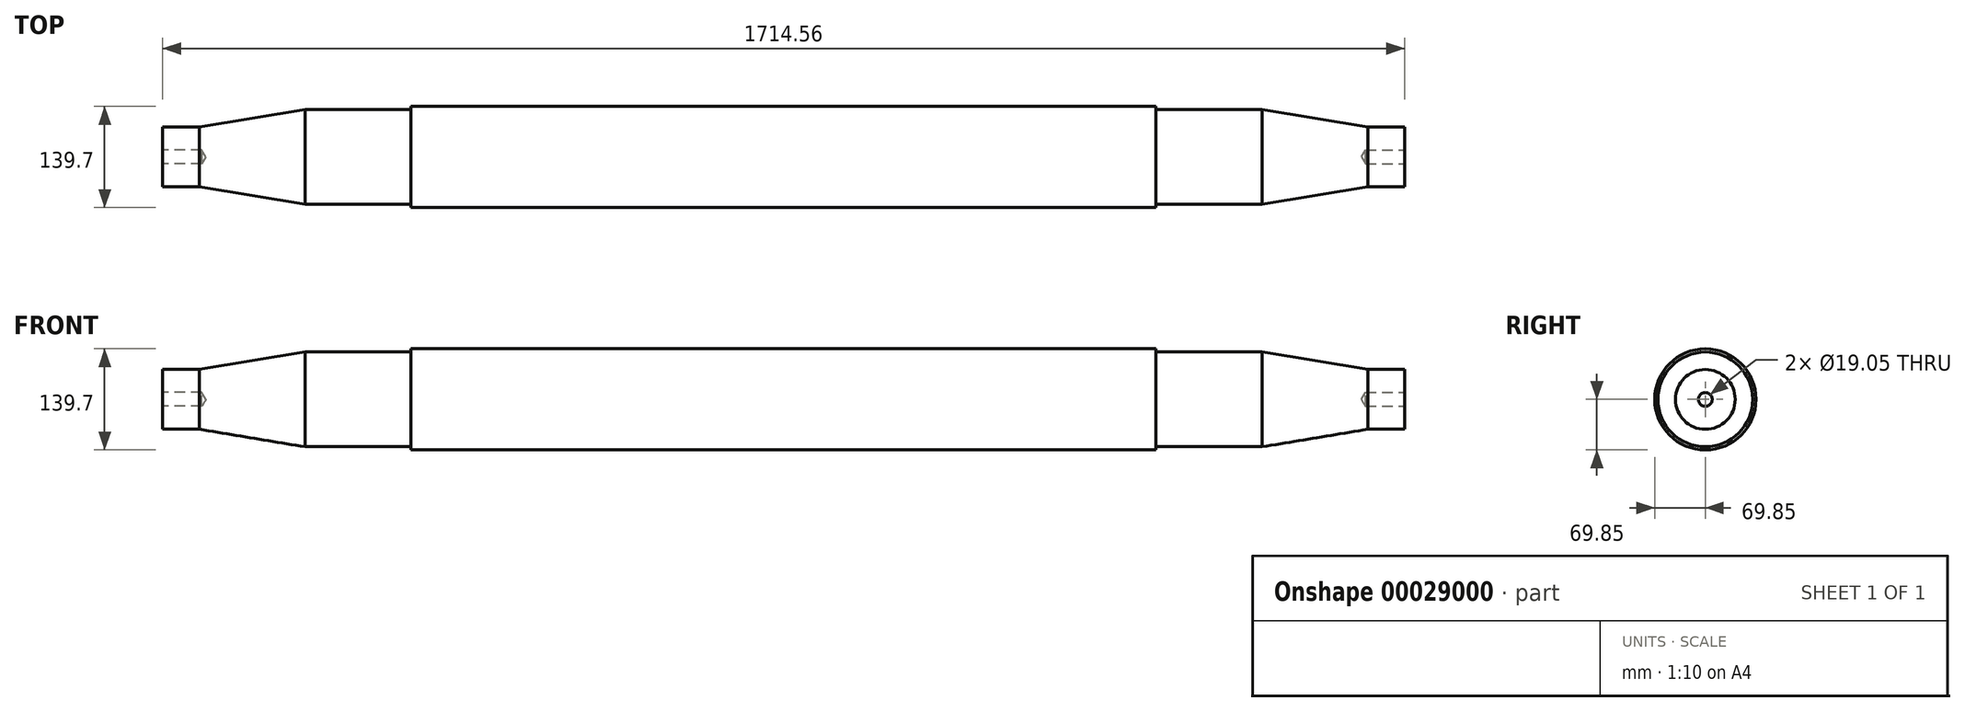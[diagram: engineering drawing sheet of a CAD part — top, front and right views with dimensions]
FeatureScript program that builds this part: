
annotation { "Feature Type Name" : "Feature", "Feature Type Description" : "" }
export const myFeature = defineFeature(function(context is Context, id is Id, definition is map)
    precondition{}
    {
        {
            var Q0;
            Q0=qCreatedBy(makeId("Right.planeOp"),FACE);
            var sketch = newSketch(context, id + "F0", { "sketchPlane" : qUnion([Q0])});
            skCircle(sketch, "E0", {"center": v(0, 0) * mm, "radius": 69.85 * mm});
            skSolve(sketch);
        }
        {
            var Q0;
            Q0 = qSketchRegion(id + "F0", true);
            extrude(context, id + "F1", {"entities" : qUnion([Q0]), "endBound" : BoundingType.SYMMETRIC, "depth" : 1028.7 * mm});
        }
        {
            var Q0;
            Q0=makeQuery(id+"F1.opExtrude","CAP_FACE",FACE,{"disambiguationData":[OSD([sQuery(id+"F0.wireOp",EDGE,"E0")])],"isStart":false});
            var sketch = newSketch(context, id + "F2", { "sketchPlane" : qUnion([Q0])});
            skCircle(sketch, "E1", {"center": v(0, 0) * mm, "radius": 65.4 * mm});
            skSolve(sketch);
        }
        {
            var Q0;
            Q0 = qSketchRegion(id + "F2", true);
            extrude(context, id + "F3", {"entities" : qUnion([Q0]), "depth" : 146.08 * mm});
        }
        {
            var Q0;
            Q0=makeQuery(id+"F3.opExtrude","CAP_FACE",FACE,{"disambiguationData":[OSD([sQuery(id+"F2.wireOp",EDGE,"E1")])],"isStart":false});
            cPlane(context, id + "F4", {"entities" : qUnion([Q0]), "cplaneType" : CPlaneType.OFFSET, "offset" : 146.05 * mm, "width" : 152.4 * mm, "height" : 152.4 * mm});
        }
        {
            var Q0;
            Q0=qCreatedBy(id+"F4.planeOp",FACE);
            var sketch = newSketch(context, id + "F5", { "sketchPlane" : qUnion([Q0])});
            skCircle(sketch, "E2", {"center": v(0, 0) * mm, "radius": 41.28 * mm});
            skSolve(sketch);
        }
        {
            var Q1;
            Q1=makeQuery(id+"F3.opExtrude","CAP_FACE",FACE,{"disambiguationData":[OSD([sQuery(id+"F2.wireOp",EDGE,"E1")])],"isStart":false});
            var Q2;
            Q2=makeQuery(id+"F5.imprint","IMPRINT",FACE,{"disambiguationData":[TD([[makeQuery(id+"F5.imprint","IMPRINT",EDGE,{"derivedFrom":sQuery(id+"F5.wireOp",EDGE,"E2")}),1.0]])]});
            loft(context, id + "F6", {"operationType" : NewBodyOperationType.ADD, "sheetProfilesArray" : [{ "sheetProfileEntities" : qUnion([Q1]) }, { "sheetProfileEntities" : qUnion([Q2]) }]});
        }
        {
            var Q0;
            Q0=makeQuery(id+"F6.opLoft","CAP_FACE",FACE,{"disambiguationData":[OSD([makeQuery(id+"F5.imprint","IMPRINT",FACE,{"disambiguationData":[TD([[makeQuery(id+"F5.imprint","IMPRINT",EDGE,{"derivedFrom":sQuery(id+"F5.wireOp",EDGE,"E2")}),1.0]])]})])],"isStart":true});
            var sketch = newSketch(context, id + "F7", { "sketchPlane" : qUnion([Q0])});
            skCircle(sketch, "E3.0", {"center": v(0, 0) * mm, "radius": 41.28 * mm});
            skSolve(sketch);
        }
        {
            var Q0;
            Q0 = qSketchRegion(id + "F7", true);
            extrude(context, id + "F8", {"entities" : qUnion([Q0]), "operationType" : NewBodyOperationType.ADD, "depth" : 50.8 * mm});
        }
        {
            var Q0;
            Q0=makeQuery(id+"F8.opExtrude","CAP_FACE",FACE,{"disambiguationData":[OSD([sQuery(id+"F7.wireOp",EDGE,"E3.0")])],"isStart":false});
            var sketch = newSketch(context, id + "F9", { "sketchPlane" : qUnion([Q0])});
            skPoint(sketch, "E4", {"position": v(0, 0) * mm});
            skSolve(sketch);
        }
        {
            var Q0;
            Q0=sQuery(id+"F9.wireOp",VERTEX,"E4");
            var Q1;
            Q1=makeQuery(id+"F3.opExtrude","SWEPT_BODY",BODY,{"disambiguationData":[OSD([sQuery(id+"F2.wireOp",EDGE,"E1")])]});
            hole(context, id + "F10", {"style" : HoleStyle.SIMPLE, "holeDiameter" : 19.05 * mm, "endStyle" : HoleEndStyle.BLIND, "holeDepth" : 53.97 * mm, "locations" : qUnion([Q0]), "scope" : qUnion([Q1])});
        }
        {
            var Q0;
            Q0=makeQuery(id+"F3.opExtrude","SWEPT_BODY",BODY,{"disambiguationData":[OSD([sQuery(id+"F2.wireOp",EDGE,"E1")])]});
            var Q1;
            Q1=qCreatedBy(makeId("Right.planeOp"),FACE);
            mirror(context, id + "F11", {"operationType" : NewBodyOperationType.ADD, "entities" : qUnion([Q0]), "mirrorPlane" : qUnion([Q1])});
        }
    });
